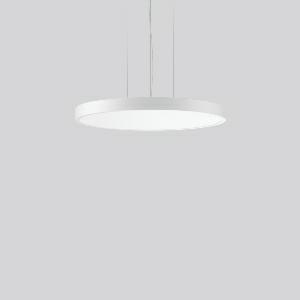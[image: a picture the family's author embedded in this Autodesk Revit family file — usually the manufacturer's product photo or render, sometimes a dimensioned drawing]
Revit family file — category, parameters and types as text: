
# Revit family: triona_round_p_312386_002_1_76_0076
name_source: partatom
category: Lighting Fixtures
units: mm (PartAtom-declared; Revit-internal decimal feet)

## family parameters
Cut with Voids When Loaded = No
Host = Face
Light Source = No
Part Type = Normal
Room Calculation Point = No
Round Connector Dimension = Use Diameter
Shared = No

## types (1)
- TRIONA round P (1 x LED Modul 840, 9650 lm, 4000)
    Apparent Load = 106 VA
    CIE Flux Codes = 49 80 96 72 100
    Color Rendering = 80
    Color Temperature = 4000
    Default Elevation = 1800 mm
    Description = Series: TRIONA round
Decorative round LED pendant-mounted surface luminaire. Flat, seamless frame: aluminium extrusion profile, powder coated. Cover made of sheet steel, powder-coated. Canopy made of aluminium, powder-coated. Direct light emission through a diffuser plastic opal. Indirect light emission through a flush diffuser made of satin-finish plastic. Lightguide and diffuser made of non-yellowing plastic (PMMA). Lateral light emission (RZB SIDELITE technology) for above-average homogeneous light distribution. Direct 70%, indirect 30% light emission. 3-point steel cable suspension, steplessly adjustable. Easy installation with transparent, adjustable pendant cable and canopy with magnetic fixing. Driver integrated. 
Colour: traffic white, matt (RAL 9016)
Diameter: 681 mm
Height: 52 mm
Suspension length: 500-1200 mm
Lamp: LED
Socket: without socket
Colour temperature: 4000K
Colour rendering index (CRI): 80
System power: 106 W
Rated luminous flux: 9650 lm
Luminous efficiency: 91 lm/W
Control gear: Converter, dimmable, DALI
Protection class: I
Type of protection: IP 20
    Height = 52 mm  [stored 0.170604 ft]
    Lamp = 1 x LED Modul 840
    Lamp Light Flux = 9650 lm
    Lamp count = 1
    Length = 681 mm
    Lifetime = 50000 h
    Luminous efficacy = 91 lm/W
    Manufacturer = RZB
    ModVariant = No
    Model = 312386.002.1.76
    Mounting Place = Ceiling
    Mounting Type = Pendant
    Number of Poles = 1
    OnlyDefault = Yes
    Power Factor = 1
    Product Name = TRIONA round P
    Product group = Pendant modular luminaires
    ProductGroupID = 906
    Protection Class = Protection class I
    Protection Degree = IP 20
    RLX_Detail_Level = 1
    RLX_Emergency_Light_Flux = 0 lm
    RLX_Emergency_Type = 0
    RLX_Emergency_Type_DB = No
    RlxData = <blob elided: 36773 chars, md5=d253472a>
    Socket = socket
    Standby Power = 0 W
    System Light Flux = 9650 lm
    System Power = 106 W
    Type Comments = Product without accessories
    Type Image = 312386.002.jpg
    URL = http://relux.com
    VarID = ---
    Voltage = 230 V
    Voltage Range = 220-240 V
    Weight = 0.00 kg
    Width = 0 mm  [stored 0 ft]

note: [stored X ft] marks values corroborated as IEEE doubles in the binary element streams (Revit-internal decimal feet)

## geometry (parser evidence)
native form markers: Blend x4, Sweep x11
no freeform markers — native parametric forms only
